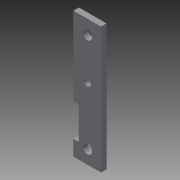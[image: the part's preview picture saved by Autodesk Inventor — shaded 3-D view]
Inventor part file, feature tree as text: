
AUTODESK INVENTOR PART (.ipt)
format: ipt  version: 2015 (Build 190159000, 159)  size: 118,784 bytes
history: native  units: mm
features: extrude x1, sketch x1
ambient origin geometry x8: Origin, YZ Plane, XZ Plane, XY Plane, X Axis, Y Axis, Z Axis, Center Point
bodies: Solid1 (feature_tree)
feature tree (2):
  extrude  "Extrusion1"  Depth=23.5mm
  sketch  "Sketch1"  dims[d0=21.0mm d1=23.5mm d2=10.5mm d3=11.75mm d5=23.5mm d6=5.0mm d7=23.5mm d9=70.5mm d40=21.625mm d41=70.5mm d42=91.5mm d43=10.0mm d44=10.0mm d45=7.0mm d46=10.0mm d47=10.0mm d48=90.0deg d50=7.0mm d51=10.0mm d52=10.0mm d53=7.0mm d54=10.0mm d55=10.0mm d56=7.0mm d60=30.0mm d61=30.0mm d62=5.0mm d63=5.0mm d65=20.0mm d66=4.0mm d67=0.0mm]
